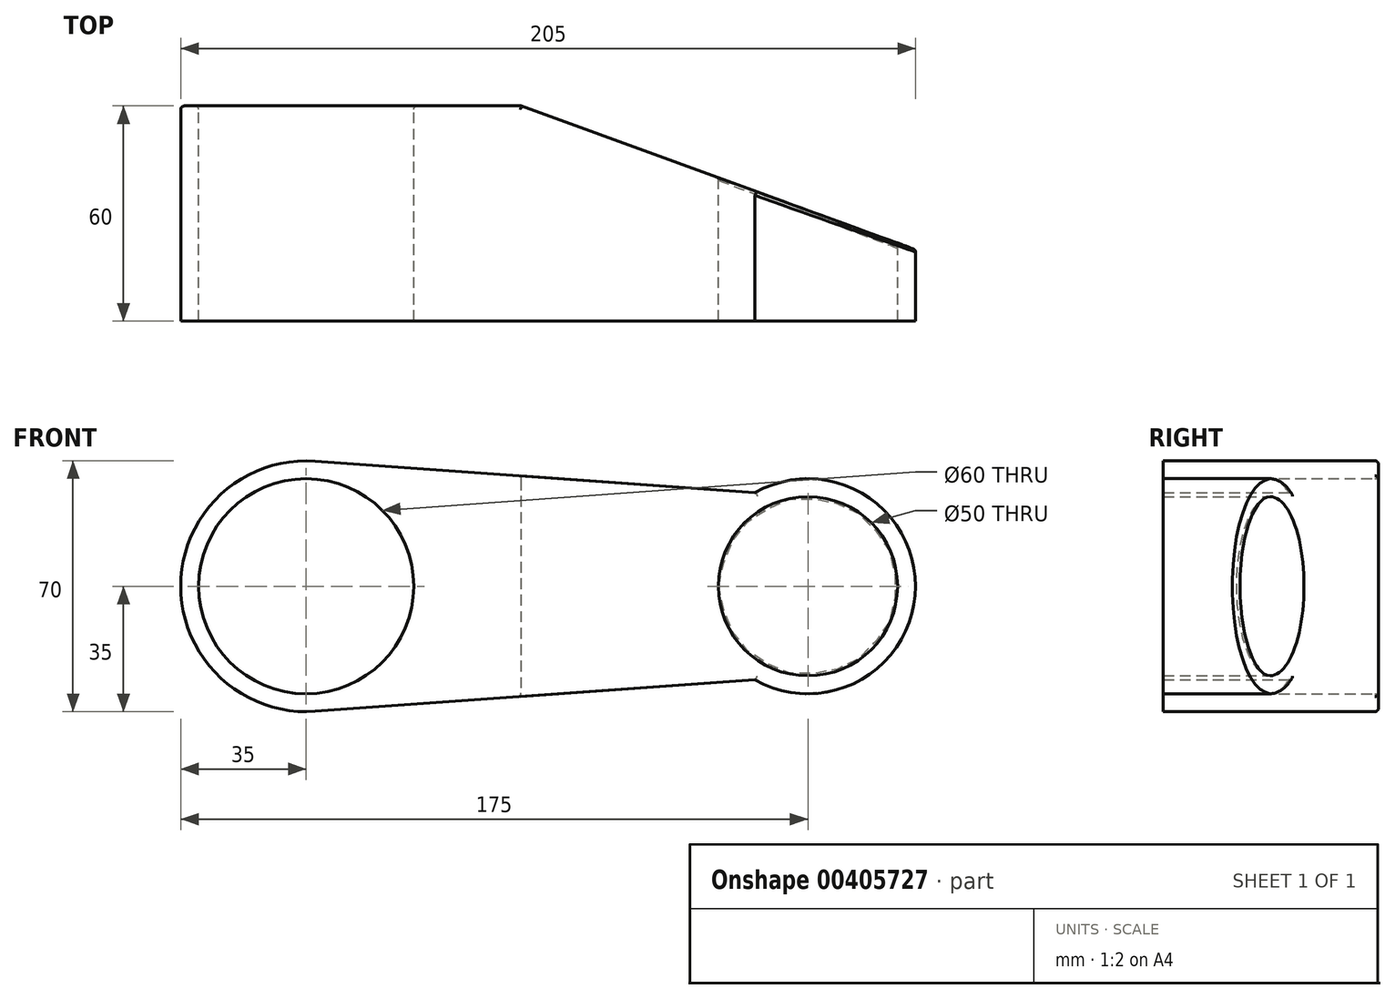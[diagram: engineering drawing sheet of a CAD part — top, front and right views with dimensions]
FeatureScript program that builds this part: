
annotation { "Feature Type Name" : "Feature", "Feature Type Description" : "" }
export const myFeature = defineFeature(function(context is Context, id is Id, definition is map)
    precondition{}
    {
        {
            var Q0;
            Q0=qCreatedBy(makeId("Front.planeOp"),FACE);
            var sketch = newSketch(context, id + "F0", { "sketchPlane" : qUnion([Q0])});
            skCircle(sketch, "E0", {"center": v(0, 0) * mm, "radius": 35 * mm});
            skCircle(sketch, "E1", {"center": v(140, 0) * mm, "radius": 25 * mm});
            skLineSegment(sketch, "E2", {"start": v(2.5, 34.91) * mm, "end": v(141.79, 24.94) * mm});
            skLineSegment(sketch, "E3", {"start": v(2.5, -34.91) * mm, "end": v(141.79, -24.94) * mm});
            skCircle(sketch, "E4.0", {"center": v(0, 0) * mm, "radius": 30 * mm});
            skCircle(sketch, "E5.0", {"center": v(140, 0) * mm, "radius": 30 * mm});
            skSolve(sketch);
        }
        {
            var Q0;
            Q0 = qSketchRegion(id + "F0", true);
            extrude(context, id + "F1", {"entities" : qUnion([Q0]), "depth" : 60 * mm});
        }
        {
            var Q0;
            Q0=qCreatedBy(makeId("Top.planeOp"),FACE);
            var sketch = newSketch(context, id + "F2", { "sketchPlane" : qUnion([Q0])});
            skLineSegment(sketch, "E6", {"start": v(194, 0) * mm, "end": v(194, -48.8) * mm});
            skLineSegment(sketch, "E7", {"start": v(194, -48.8) * mm, "end": v(59.9, 0) * mm});
            skLineSegment(sketch, "E8", {"start": v(59.9, 0) * mm, "end": v(194, 0) * mm});
            skSolve(sketch);
        }
        {
            var Q0;
            Q0 = qSketchRegion(id + "F2", true);
            extrude(context, id + "F3", {"entities" : qUnion([Q0]), "operationType" : NewBodyOperationType.REMOVE, "endBound" : BoundingType.SYMMETRIC, "depth" : 90 * mm});
        }
        {
            var Q0;
            Q0=makeQuery(id+"F3.boolean.opBoolean","INTERSECT",EDGE,{"derivedFrom":[makeQuery(id+"F1.opExtrude","SWEPT_FACE",FACE,{"disambiguationData":[OSD([sQuery(id+"F0.wireOp",EDGE,"E1")])]}),makeQuery(id+"F3.opExtrude","SWEPT_FACE",FACE,{"disambiguationData":[OSD([sQuery(id+"F2.wireOp",EDGE,"E7")])]})]});
            var Q1;
            Q1=makeQuery(id+"F3.boolean.opBoolean","INTERSECT",EDGE,{"derivedFrom":[makeQuery(id+"F1.opExtrude","SWEPT_FACE",FACE,{"disambiguationData":[OSD([sQuery(id+"F0.wireOp",EDGE,"E2")])]}),makeQuery(id+"F3.opExtrude","SWEPT_FACE",FACE,{"disambiguationData":[OSD([sQuery(id+"F2.wireOp",EDGE,"E7")])]})]});
            var Q2;
            Q2=makeQuery(id+"F3.boolean.opBoolean","INTERSECT",EDGE,{"derivedFrom":[makeQuery(id+"F1.opExtrude","SWEPT_FACE",FACE,{"disambiguationData":[OSD([sQuery(id+"F0.wireOp",EDGE,"E5.0")])]}),makeQuery(id+"F3.opExtrude","SWEPT_FACE",FACE,{"disambiguationData":[OSD([sQuery(id+"F2.wireOp",EDGE,"E7")])]})]});
            var Q3;
            Q3=makeQuery(id+"F3.boolean.opBoolean","INTERSECT",EDGE,{"derivedFrom":[makeQuery(id+"F1.opExtrude","SWEPT_FACE",FACE,{"disambiguationData":[OSD([sQuery(id+"F0.wireOp",EDGE,"E3")])]}),makeQuery(id+"F3.opExtrude","SWEPT_FACE",FACE,{"disambiguationData":[OSD([sQuery(id+"F2.wireOp",EDGE,"E7")])]})]});
            var Q4;
            Q4=makeQuery(id+"F1.opExtrude","CAP_EDGE",EDGE,{"disambiguationData":[OSD([sQuery(id+"F0.wireOp",EDGE,"E4.0")])],"isStart":true});
            var Q5;
            Q5=makeQuery(id+"F1.opExtrude","CAP_EDGE",EDGE,{"disambiguationData":[OSD([sQuery(id+"F0.wireOp",EDGE,"E2")])],"isStart":true});
            var Q6;
            Q6=makeQuery(id+"F1.opExtrude","CAP_EDGE",EDGE,{"disambiguationData":[OSD([sQuery(id+"F0.wireOp",EDGE,"E0")])],"isStart":true});
            var Q7;
            Q7=makeQuery(id+"F1.opExtrude","CAP_EDGE",EDGE,{"disambiguationData":[OSD([sQuery(id+"F0.wireOp",EDGE,"E3")])],"isStart":true});
            fillet(context, id + "F4", {"entities" : qUnion([Q0, Q1, Q2, Q3, Q4, Q5, Q6, Q7]), "radius" : 1 * mm, "tangentPropagation" : true, "allowEdgeOverflow" : false});
        }
    });
